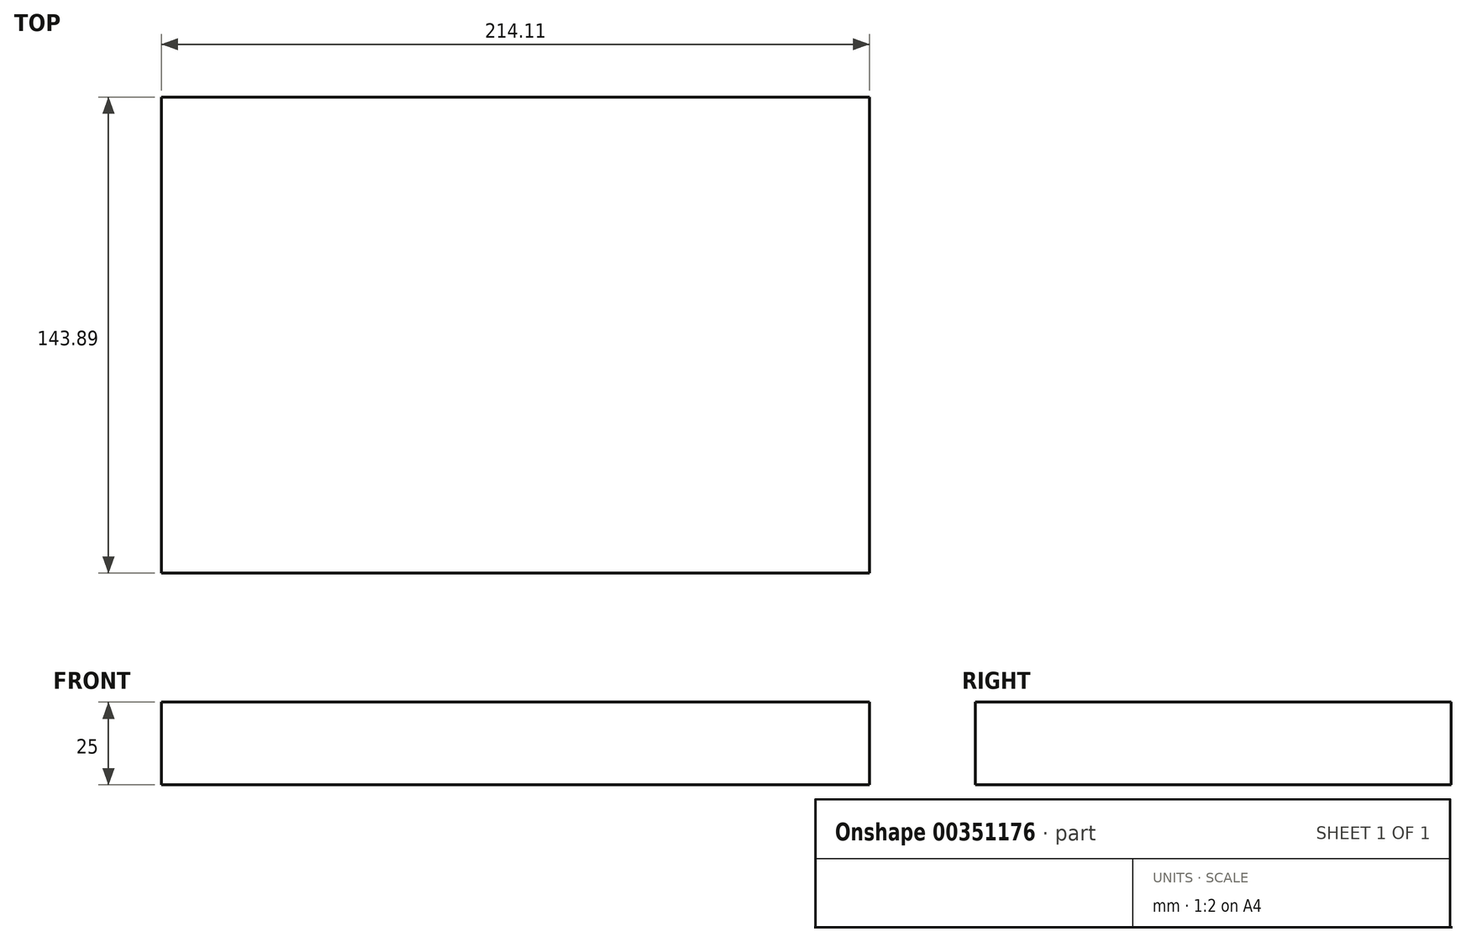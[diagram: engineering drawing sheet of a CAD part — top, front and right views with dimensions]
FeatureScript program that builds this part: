
annotation { "Feature Type Name" : "Feature", "Feature Type Description" : "" }
export const myFeature = defineFeature(function(context is Context, id is Id, definition is map)
    precondition{}
    {
        {
            var Q0;
            Q0=qCreatedBy(makeId("Top.planeOp"),FACE);
            var sketch = newSketch(context, id + "F0", { "sketchPlane" : qUnion([Q0])});
            skLineSegment(sketch, "E0.bottom", {"start": v(-93.81, 68.95) * mm, "end": v(120.3, 68.95) * mm});
            skLineSegment(sketch, "E0.top", {"start": v(-93.81, -74.94) * mm, "end": v(120.3, -74.94) * mm});
            skLineSegment(sketch, "E0.left", {"start": v(-93.81, 68.95) * mm, "end": v(-93.81, -74.94) * mm});
            skLineSegment(sketch, "E0.right", {"start": v(120.3, 68.95) * mm, "end": v(120.3, -74.94) * mm});
            skText(sketch, "E1", { "text": "Tal\n", "fontName": "OpenSans-Regular.ttf"});
            const initialGuessF0  = {"E1": [-0.06968, -0.02776, 1, 0, 0.07839]};
            skSetInitialGuess(sketch, initialGuessF0);
            skSolve(sketch);
        }
        {
            var Q0;
            Q0=sQuery(id+"F0.wireOp",EDGE,"E0.bottom");
            var Q1;
            Q1=sQuery(id+"F0.wireOp",EDGE,"E0.top");
            var Q2;
            Q2=sQuery(id+"F0.wireOp",EDGE,"E0.left");
            var Q3;
            Q3=sQuery(id+"F0.wireOp",EDGE,"E0.right");
            extrude(context, id + "F1", {"bodyType" : ToolBodyType.SURFACE, "surfaceEntities" : qUnion([Q0, Q1, Q2, Q3]), "depth" : 25 * mm});
        }
    });
